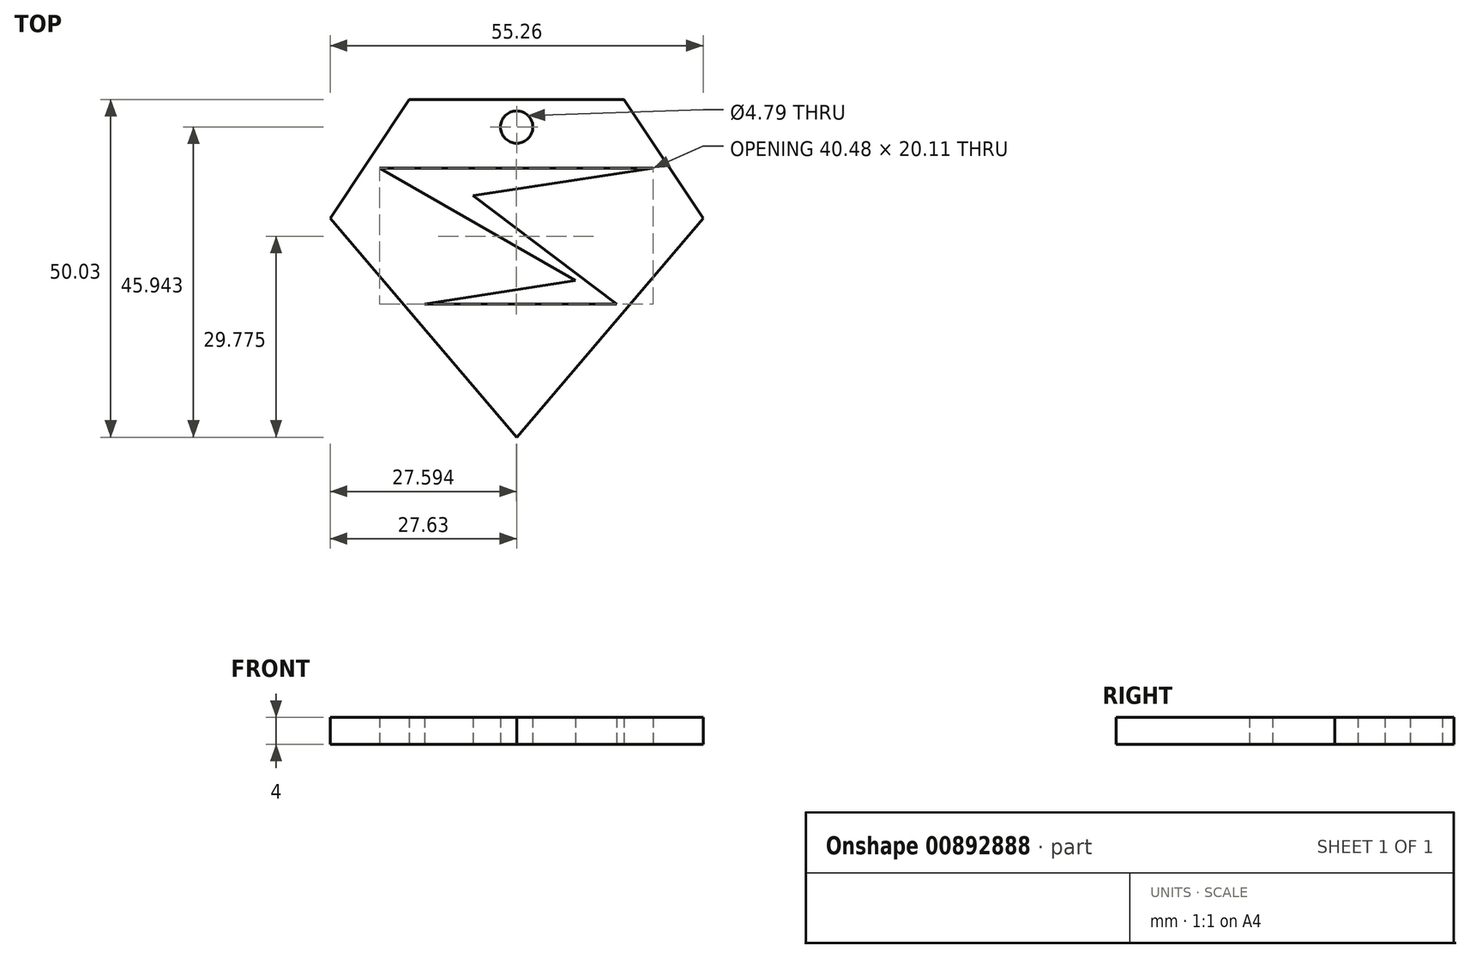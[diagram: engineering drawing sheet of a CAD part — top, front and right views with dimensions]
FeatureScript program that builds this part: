
annotation { "Feature Type Name" : "Feature", "Feature Type Description" : "" }
export const myFeature = defineFeature(function(context is Context, id is Id, definition is map)
    precondition{}
    {
        {
            var Q0;
            Q0=qCreatedBy(makeId("Top.planeOp"),FACE);
            var sketch = newSketch(context, id + "F0", { "sketchPlane" : qUnion([Q0])});
            skLineSegment(sketch, "E0", {"start": v(0, 30.3) * mm, "end": v(15.89, 30.3) * mm});
            skLineSegment(sketch, "E1", {"start": v(15.89, 30.3) * mm, "end": v(27.63, 12.7) * mm});
            skLineSegment(sketch, "E2", {"start": v(27.63, 12.7) * mm, "end": v(0, -19.72) * mm});
            skLineSegment(sketch, "E3.MirrorCS", {"start": v(0, 30.3) * mm, "end": v(-15.89, 30.3) * mm});
            skLineSegment(sketch, "E4.MirrorCS", {"start": v(-15.89, 30.3) * mm, "end": v(-27.63, 12.7) * mm});
            skLineSegment(sketch, "E5.MirrorCS", {"start": v(-27.63, 12.7) * mm, "end": v(0, -19.72) * mm});
            skCircle(sketch, "E6", {"center": v(0, 26.22) * mm, "radius": 2.4 * mm});
            skLineSegment(sketch, "E7", {"start": v(20.2, 20.1) * mm, "end": v(-20.28, 20.1) * mm});
            skLineSegment(sketch, "E8", {"start": v(-20.28, 20.1) * mm, "end": v(14.8, 0) * mm});
            skLineSegment(sketch, "E9", {"start": v(14.8, 0) * mm, "end": v(-13.66, 0) * mm});
            skLineSegment(sketch, "E10", {"start": v(-13.66, 0) * mm, "end": v(8.75, 3.47) * mm});
            skLineSegment(sketch, "E11", {"start": v(20.2, 20.1) * mm, "end": v(-11.82, 15.26) * mm});
            skLineSegment(sketch, "E12", {"start": v(-11.82, 20.1) * mm, "end": v(14.8, 0) * mm});
            skSolve(sketch);
        }
        {
            var Q0;
            Q0 = qSketchRegion(id + "F0", true);
            extrude(context, id + "F1", {"entities" : qUnion([Q0]), "depth" : 4 * mm, "offsetDistance" : 25.4 * mm});
        }
    });
